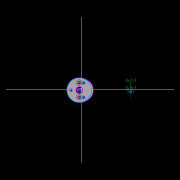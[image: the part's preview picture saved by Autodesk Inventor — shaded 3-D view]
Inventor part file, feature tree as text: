
AUTODESK INVENTOR PART (.ipt)
format: ipt  version: 2022.2 (Build 262287010, 287A)  size: 606,208 bytes
history: native  units: mm
features: extrude x27, other x22, sketch x21, pattern_circular x7, plane x7, fillet x2, move_body x2, revolve x2, loft x2, draft x2, chamfer x2, projected_geometry x1
ambient origin geometry x8: Origin, YZ Plane, XZ Plane, XY Plane, X Axis, Y Axis, Z Axis, Center Point
bodies: Solid5 (feature_tree)
feature tree (97):
  other  "CrossSection1"
  sketch  "Sketch7"  dims[d90=15.767323mm]
  other  "Roller1"
  other  "Roller2"
  sketch  "Sketch22"  dims[d167=8.972256mm]
  sketch  "Sketch2"  dims[d57=4.025mm]
  sketch  "Sketch23"  dims[d173=10.814812mm]
  other  "RevRoller1"
  fillet  "Fillet1"  Radius=13.336791mm
  pattern_circular  "Circular Pattern13"  Count=360  [1 undecoded]
  move_body  "Move Body7"
  revolve  "Revolution13"  [1 undecoded]
  fillet  "Fillet3"  Radius=0.025mm
  pattern_circular  "Circular Pattern14"  Count=6  [1 undecoded]
  move_body  "Move Body6"
  revolve  "Revolution14"  Angle=30.0deg
  plane  "Work Plane7"
  sketch  "Sketch44"  dims[d349=17.374602mm]
  plane  "Work Plane8"
  loft  "Loft1"
  sketch  "Sketch46"  dims[d351=0.025mm]
  extrude  "Extrusion39"  Depth=10.0mm
  plane  "Work Plane9"
  sketch  "Sketch47"  dims[d352=0.025mm]
  extrude  "Extrusion40"  Depth=10.0mm
  extrude  "Extrusion41"  TaperAngle=30.0deg  [1 undecoded]
  extrude  "Extrusion42"  TaperAngle=90.0deg  [1 undecoded]
  sketch  "Sketch48"  dims[d354=0.025mm]
  sketch  "Sketch49"  dims[d355=17.374329mm]
  extrude  "Extrusion43"  Depth=10.0mm
  sketch  "Sketch51"  dims[d357=1.0mm]
  plane  "Work Plane14"
  plane  "Work Plane15"
  sketch  "Sketch56"  dims[d358=90.0deg]
  sketch  "Sketch57"  dims[d359=0.5mm d360=60.0mm]
  extrude  "Extrusion46"  Depth=10.0mm
  extrude  "Extrusion47"  TaperAngle=360.0deg  [1 undecoded]
  loft  "Loft2"
  extrude  "Extrusion48"  Depth=10.0mm
  extrude  "Extrusion49"  Depth=10.0mm
  extrude  "Extrusion50"  Depth=10.0mm
  extrude  "Extrusion51"  Depth=10.0mm
  extrude  "Extrusion52"  Depth=10.0mm
  other  "OuterRim_Top2"
  other  "OuterRim_Bottom2"
  extrude  "Rotor_Ring"  Depth=10.0mm
  draft  "FaceDraft2"
  sketch  "Sketch30"  dims[d201=53.5mm d232=0.0mm d233=3600.0mm]
  plane  "Work Plane5"
  other  "Rotor Featurs"
  other  "RotorRim_Bottom"
  extrude  "Extrusion24"  TaperAngle=0.0deg  [1 undecoded]
  extrude  "Extrusion25"  TaperAngle=0.0deg  [1 undecoded]
  extrude  "Extrusion26"  Depth=10.0mm
  pattern_circular  "Circular Pattern23"  [2 undecoded]
  sketch  "Sketch41"  dims[d346=0.025mm]
  extrude  "Extrusion27"  Depth=10.0mm
  extrude  "Extrusion28"  Depth=10.0mm
  pattern_circular  "Circular Pattern24"  [2 undecoded]
  extrude  "Extrusion29"  Depth=10.0mm
  extrude  "Extrusion30"  TaperAngle=90.0deg  [1 undecoded]
  extrude  "Extrusion31"  TaperAngle=90.0deg  [1 undecoded]
  pattern_circular  "Circular Pattern25"  Angle=90.0deg  [1 undecoded]
  sketch  "Sketch42"  dims[d347=0.1mm]
  extrude  "Extrusion32"  Depth=10.0mm
  extrude  "Extrusion33"  Depth=10.0mm
  extrude  "Extrusion34"  TaperAngle=0.0deg  [1 undecoded]
  extrude  "Extrusion35"  Depth=10.0mm
  pattern_circular  "Circular Pattern26"  Count=2  [1 undecoded]
  pattern_circular  "Circular Pattern27"  [2 undecoded]
  chamfer  "Chamfer1"  Distance=8.0mm
  chamfer  "Chamfer2"  Distance=13.856406mm
  draft  "FaceDraft4"
  plane  "Work Plane6"
  sketch  "Sketch43"  dims[d348=0.1mm]
  extrude  "Extrusion37"  Depth=10.0mm TaperAngle=30.0deg
  extrude  "Extrusion38"  Depth=10.0mm
  other  "2D Equation Curve1"
  sketch  "Sketch40"  dims[d343=17.374329mm d344=17.374602mm d345=0.025mm]
  other  "Work Axis6"
  other  "Work Axis7"
  other  "Work Axis8"
  other  "Work Axis9"
  other  "Work Axis10"
  other  "Work Point1"
  other  "Work Point2"
  other  "Work Point3"
  other  "Work Point4"
  other  "Work Point5"
  sketch  "Sketch45"  dims[d350=17.374329mm]
  other  "Edges1"
  sketch  "Sketch50"  dims[d356=17.374602mm]
  projected_geometry  "Projected Loop1"
  other  "Edges2"
  other  "Edges3"
  sketch  "Sketch58"  dims[d361=360.0deg d363=30.0deg]
  sketch  "Sketch59"  dims[d367=8.1mm d369=4.014775mm d370=0.025mm d371=1.0mm d372=30.0deg d373=90.0deg d374=0.5mm d375=60.0mm d376=360.0deg d378=90.0deg d379=0.1mm d380=0.025mm d381=0.025mm d382=0.025mm d383=0.025mm d384=10.461905mm d385=0.0mm d386=0.0mm d391=1.0mm d392=53.5mm d393=1.5mm d394=1.5mm d395=1.5mm d396=1.5mm d397=90.0deg d398=90.0deg d399=90.0deg d400=53.5mm d401=10.461905mm d402=0.0mm d486=0.436332mm d487=0.5mm d488=2.0mm d489=0.0mm d490=20.0mm d495=2.5mm d496=8.0mm d506=13.856406mm d507=55.5mm d508=8.0mm d509=0.05mm d510=2.5mm d511=30.0deg d512=12.0mm d513=6.0mm d514=0.2mm d515=30.0deg d516=131.0mm d517=65.5mm d518=0.2mm d519=100.0mm d520=120.0mm d521=2.0mm d522=150.0mm d530=50.0mm d531=5.5mm d532=5.5mm d533=5.5mm d534=85.75mm d535=73.5mm d536=61.25mm d537=24.5mm d538=3.0mm d539=2.4mm d540=0.0mm d541=0.0mm d542=0.0mm d543=5.5mm d544=3.0mm d545=0.0mm d546=90.0mm d547=360.0deg d549=3.0mm d550=3.0mm d551=2.4mm d552=0.0mm d553=5.230953mm d554=0.0mm d555=2.4mm d556=0.0mm d557=5.230953mm d558=0.0mm d559=5.230953mm d560=0.0mm d561=90.0mm d562=360.0deg d564=60.0mm d565=360.0deg d567=5.5mm d568=5.5mm d569=3.0mm d570=0.0mm d571=5.230953mm d572=0.0mm d573=3.0mm d574=0.0mm d575=5.230953mm d576=0.0mm d577=90.0mm d578=360.0deg d580=60.0mm d581=360.0deg d584=20.0mm d585=8.0mm d587=1.75mm d589=3.0mm d592=2.0mm d593=12.0mm d594=12.0mm d600=0.5mm d601=2.0mm d602=45.0deg d603=0.5mm d604=2.0mm d605=45.0deg d606=0.436332mm d607=0.5mm d608=0.0mm d609=20.0mm d611=360.0deg d613=0.0mm d614=0.0mm d615=20.0mm d616=3.611mm d617=0.0mm d618=90.0deg d619=0.0mm d620=90.0deg d621=2.5mm d622=7.0mm d623=0.0mm d624=0.0mm d625=50.0mm d626=5.5mm d627=3.0mm d628=5.5mm d629=43.459mm d630=0.0mm d631=52.538mm d632=0.0mm d633=4.8mm d634=0.0mm d635=3.0mm d636=3.0mm d637=0.0mm d638=0.0mm d649=17.431mm d650=5.231mm d651=1.0mm d652=0.0mm d653=1.0mm d654=0.0mm d655=0.0mm d656=90.0deg d657=0.0mm d658=90.0deg d659=0.0mm d660=0.0mm d661=10.0mm d662=0.0mm d663=0.0mm d664=0.0mm d665=5.5mm d666=5.5mm d667=3.5mm d668=0.0mm d669=5.5mm d670=5.5mm d671=5.5mm d672=3.1mm d673=0.0mm d16=0.872665mm d17=0.872665mm d49=0.872665mm d50=0.872665mm d51=0.872665mm d52=0.872665mm d236=0.5mm d237=0.872665mm d238=0.5mm d239=0.872665mm d282=1.0mm d283=1.0mm d284=1.0mm d285=0.15mm d286=0.25mm d287=0.375mm d288=14.3117mm d289=0.75mm d290=20.594885mm d291=0.0625mm d292=0.75mm d293=0.375mm d405=0.5mm d406=0.872665mm d407=0.5mm d408=0.872665mm d413=0.5mm d414=0.872665mm d415=0.5mm d416=0.872665mm d417=0.5mm d418=0.872665mm d419=0.5mm d420=0.872665mm d421=0.872665mm d431=0.5mm d432=0.872665mm d433=0.5mm d434=0.872665mm d471=0.5mm d472=0.872665mm d473=0.5mm d474=0.872665mm d497=0.5mm d498=0.872665mm d499=0.5mm d500=0.872665mm d590=0.5mm d591=0.872665mm d646=0.5mm d647=0.872665mm d648=0.5mm]
note: 19 required parameter values undecoded (feature->parameter linkage not recoverable at this tier; creation-order binding heuristic only, values carry confidence <= 0.55)